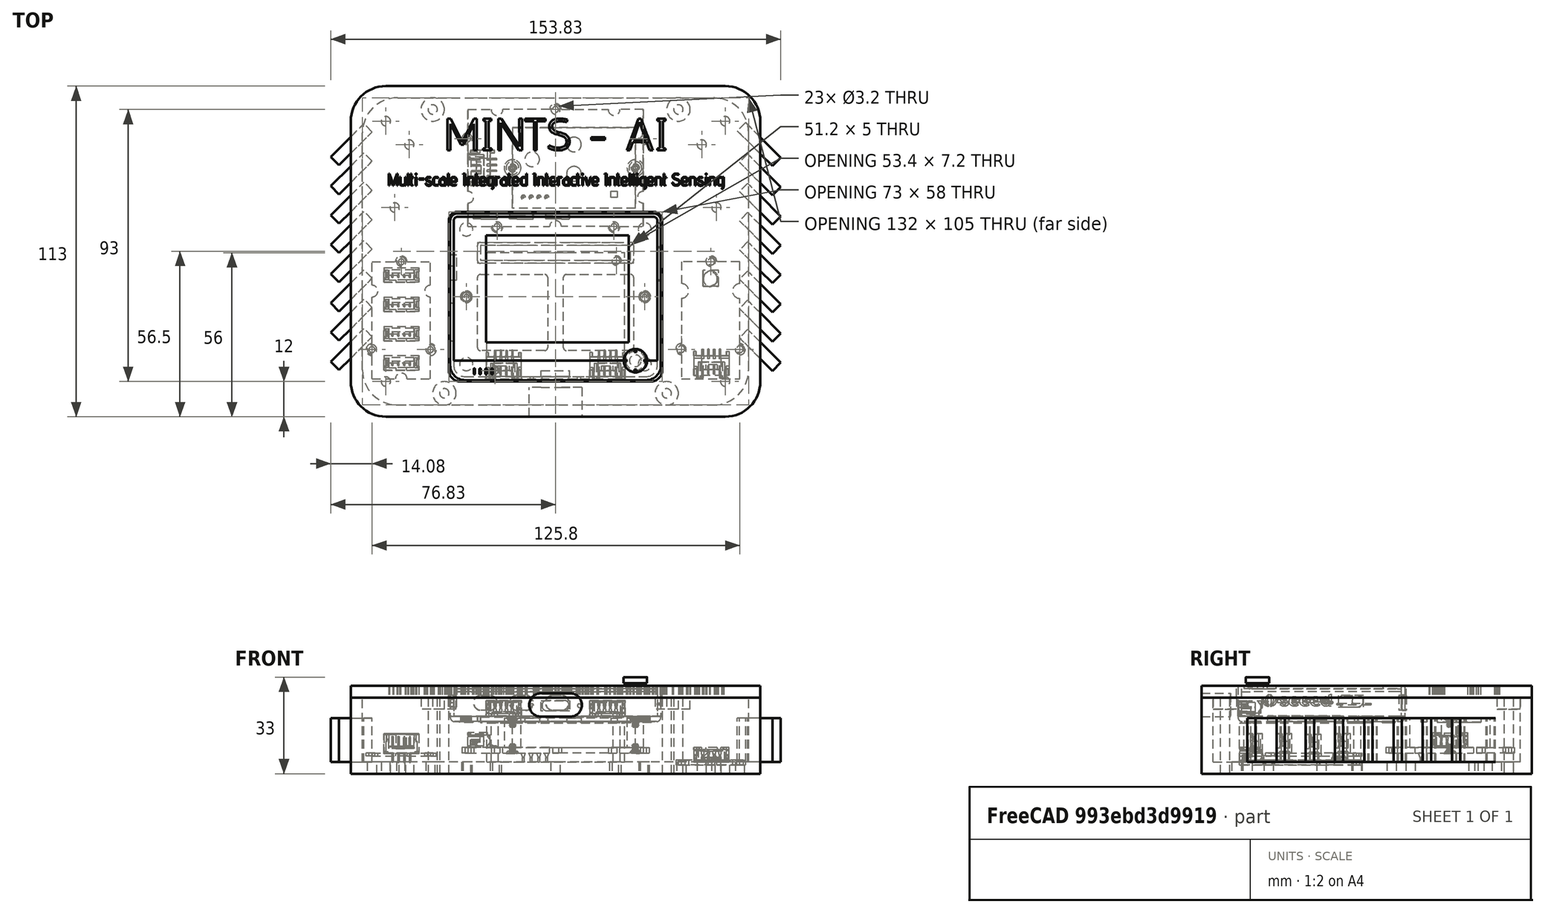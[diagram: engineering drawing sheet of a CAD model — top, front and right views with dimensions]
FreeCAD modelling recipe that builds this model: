
FCSTD DOCUMENT  (FreeCAD 0.20R29177 (Git))
Label: outBuildCopy2
License: All rights reserved
LicenseURL: http://en.wikipedia.org/wiki/All_rights_reserved
objects: Part::Cylinder×59, Part::Box×43, Part::Cut×33, Part::MultiFuse×23, Part::Feature×4, Part::Part2DObjectPython×2, Part::Extrusion×2
note: 166 computed .brp shape members not serialized (recipe doc carries the construction recipe); baked Part::Feature solids carry a one-line shape summary decoded from their .brp

FEATURE [Part::Feature] Feature  label="Grove I2C hub"
  Placement = pos=(15,60,9) rot=(0,0,1;3.14159rad)
  shape: bbox 24 x 42 x 9.849 mm, 365 faces, 5 solids (baked)
FEATURE [Part::Feature] Feature001  label="Grove_BME280"
  Placement = pos=(113,14,3) rot=(0.57735,0.57735,0.57735;2.0944rad)
  shape: bbox 23.8 x 41.9 x 6.016 mm, 221 faces, 2 solids (baked)
FEATURE [Part::Box] Box043  label="ips7100"
  AttacherType = Attacher::AttachEngine3D
  Height = 13.4
  Length = 47.1
  Width = 43.1
FEATURE [Part::Cylinder] Cylinder045  label="Cylinder"
  Angle = 360
  AttacherType = Attacher::AttachEngine3D
  FirstAngle = 0
  Height = 20
  Placement = pos=(2.75,2.75,0) rot=(0,0,1;0rad)
  Radius = 1.2
  SecondAngle = 0
FEATURE [Part::Cylinder] Cylinder046
  Angle = 360
  AttacherType = Attacher::AttachEngine3D
  FirstAngle = 0
  Height = 20
  Placement = pos=(44.35,40.35,0) rot=(0,0,1;0rad)
  Radius = 1.2
  SecondAngle = 0
FEATURE [Part::MultiFuse] Fusion030
  Shapes = -> [Cylinder045,Cylinder046]
FEATURE [Part::Cut] Cut012  label="ips7100s"
  Base = -> Box043
  Placement = pos=(46.5,13,4) rot=(0,0,1;0rad)
  Tool = -> Fusion030
FEATURE [Part::Feature] Feature002  label="Wio Terminal"
  Placement = pos=(70,41,30) rot=(0,0,1;0rad)
  shape: bbox 73.03 x 57.91 x 15.61 mm, 2405 faces, 30 solids (baked)
FEATURE [Part::Feature] Feature003  label="Seed Grove SCD30"
  Placement = pos=(40,65,9) rot=(1,0,0;4.71239rad)
  shape: bbox 64 x 44 x 15.1 mm, 422 faces, 13 solids (baked)
FEATURE [Part::Box] Box  label="base"
  AttacherType = Attacher::AttachEngine3D
  Height = 4
  Length = 140
  Width = 113
FEATURE [Part::Cylinder] Cylinder047  label="Cylinder048"
  Angle = 360
  AttacherType = Attacher::AttachEngine3D
  FirstAngle = 0
  Height = 10
  Placement = pos=(7.25,23,0) rot=(0,0,1;0rad)
  Radius = 1.6
  SecondAngle = 0
FEATURE [Part::Cylinder] Cylinder048  label="Cylinder049"
  Angle = 360
  AttacherType = Attacher::AttachEngine3D
  FirstAngle = 0
  Height = 10
  Placement = pos=(27.25,23,0) rot=(0,0,1;0rad)
  Radius = 1.6
  SecondAngle = 0
FEATURE [Part::Cylinder] Cylinder049  label="Cylinder050"
  Angle = 360
  AttacherType = Attacher::AttachEngine3D
  FirstAngle = 0
  Height = 10
  Placement = pos=(17.25,53,0) rot=(0,0,1;0rad)
  Radius = 1.6
  SecondAngle = 0
FEATURE [Part::MultiFuse] Fusion  label="i2cCuts"
  Shapes = -> [Cylinder047,Cylinder048,Cylinder049]
FEATURE [Part::Cylinder] Cylinder050  label="Cylinder051"
  Angle = 360
  AttacherType = Attacher::AttachEngine3D
  FirstAngle = 0
  Height = 10
  Placement = pos=(7.25,23,0) rot=(0,0,1;0rad)
  Radius = 1.6
  SecondAngle = 0
FEATURE [Part::Cylinder] Cylinder051  label="Cylinder052"
  Angle = 360
  AttacherType = Attacher::AttachEngine3D
  FirstAngle = 0
  Height = 10
  Placement = pos=(27.25,23,0) rot=(0,0,1;0rad)
  Radius = 1.6
  SecondAngle = 0
FEATURE [Part::Cylinder] Cylinder052  label="Cylinder053"
  Angle = 360
  AttacherType = Attacher::AttachEngine3D
  FirstAngle = 0
  Height = 10
  Placement = pos=(17.25,53,0) rot=(0,0,1;0rad)
  Radius = 1.6
  SecondAngle = 0
FEATURE [Part::MultiFuse] Fusion031  label="scdCuts001"
  Placement = pos=(105.8,0,0) rot=(0,0,1;0rad)
  Shapes = -> [Cylinder050,Cylinder051,Cylinder052]
FEATURE [Part::Cylinder] Cylinder053  label="Cylinder054"
  Angle = 360
  AttacherType = Attacher::AttachEngine3D
  FirstAngle = 0
  Height = 20
  Placement = pos=(2.75,2.75,0) rot=(0,0,1;0rad)
  Radius = 1.6
  SecondAngle = 0
FEATURE [Part::Cylinder] Cylinder054  label="Cylinder055"
  Angle = 360
  AttacherType = Attacher::AttachEngine3D
  FirstAngle = 0
  Height = 20
  Placement = pos=(44.35,40.35,0) rot=(0,0,1;0rad)
  Radius = 1.6
  SecondAngle = 0
FEATURE [Part::MultiFuse] Fusion032  label="ipsCuts"
  Placement = pos=(46.5,13,0) rot=(0,0,1;0rad)
  Shapes = -> [Cylinder053,Cylinder054]
FEATURE [Part::Cylinder] Cylinder055  label="Cylinder056"
  Angle = 360
  AttacherType = Attacher::AttachEngine3D
  FirstAngle = 0
  Height = 10
  Placement = pos=(50,65,0) rot=(0,0,1;0rad)
  Radius = 1.6
  SecondAngle = 0
FEATURE [Part::Cylinder] Cylinder056  label="Cylinder057"
  Angle = 360
  AttacherType = Attacher::AttachEngine3D
  FirstAngle = 0
  Height = 10
  Placement = pos=(90,65,0) rot=(0,0,1;0rad)
  Radius = 1.6
  SecondAngle = 0
FEATURE [Part::Cylinder] Cylinder057  label="Cylinder058"
  Angle = 360
  AttacherType = Attacher::AttachEngine3D
  FirstAngle = 0
  Height = 10
  Placement = pos=(100,95,0) rot=(0,0,1;0rad)
  Radius = 1.6
  SecondAngle = 0
FEATURE [Part::Cylinder] Cylinder058  label="Cylinder059"
  Angle = 360
  AttacherType = Attacher::AttachEngine3D
  FirstAngle = 0
  Height = 10
  Placement = pos=(40,95,0) rot=(0,0,1;0rad)
  Radius = 1.6
  SecondAngle = 0
FEATURE [Part::Cylinder] Cylinder059  label="Cylinder060"
  Angle = 360
  AttacherType = Attacher::AttachEngine3D
  FirstAngle = 0
  Height = 10
  Placement = pos=(70,105,0) rot=(0,0,1;0rad)
  Radius = 1.6
  SecondAngle = 0
FEATURE [Part::MultiFuse] Fusion033  label="scdCuts"
  Shapes = -> [Cylinder055,Cylinder056,Cylinder057,Cylinder058,Cylinder059]
FEATURE [Part::Cylinder] Cylinder060  label="Cylinder061"
  Angle = 360
  AttacherType = Attacher::AttachEngine3D
  FirstAngle = 0
  Height = 20
  Placement = pos=(39.5,41,0) rot=(0,0,1;0rad)
  Radius = 1.6
  SecondAngle = 0
FEATURE [Part::Cylinder] Cylinder061  label="Cylinder062"
  Angle = 360
  AttacherType = Attacher::AttachEngine3D
  FirstAngle = 0
  Height = 20
  Placement = pos=(100.5,41,0) rot=(0,0,1;0rad)
  Radius = 1.6
  SecondAngle = 0
FEATURE [Part::MultiFuse] Fusion034  label="wioCuts"
  Shapes = -> [Cylinder060,Cylinder061]
FEATURE [Part::MultiFuse] Fusion035  label="cuts"
  Shapes = -> [Fusion,Fusion031,Fusion032,Fusion033,Fusion034]
FEATURE [Part::Cut] Cut  label="base001"
  Base = -> Box
  Tool = -> Fusion035
FEATURE [Part::Cylinder] Cylinder062  label="Cylinder063"
  Angle = 360
  AttacherType = Attacher::AttachEngine3D
  FirstAngle = 0
  Height = 10
  Placement = pos=(12,12,0) rot=(0,0,1;0rad)
  Radius = 1.6
  SecondAngle = 0
FEATURE [Part::Cylinder] Cylinder063  label="Cylinder064"
  Angle = 360
  AttacherType = Attacher::AttachEngine3D
  FirstAngle = 0
  Height = 10
  Placement = pos=(128,12,0) rot=(0,0,1;0rad)
  Radius = 1.6
  SecondAngle = 0
FEATURE [Part::Cylinder] Cylinder064  label="Cylinder065"
  Angle = 360
  AttacherType = Attacher::AttachEngine3D
  FirstAngle = 0
  Height = 10
  Placement = pos=(12,101,0) rot=(0,0,1;0rad)
  Radius = 1.6
  SecondAngle = 0
FEATURE [Part::Cylinder] Cylinder065  label="Cylinder066"
  Angle = 360
  AttacherType = Attacher::AttachEngine3D
  FirstAngle = 0
  Height = 10
  Placement = pos=(128,101,0) rot=(0,0,1;0rad)
  Radius = 1.6
  SecondAngle = 0
FEATURE [Part::MultiFuse] Fusion036  label="outerCuts"
  Shapes = -> [Cylinder062,Cylinder063,Cylinder064,Cylinder065]
FEATURE [Part::Cut] Cut013  label="base003"
  Base = -> Cut
  Tool = -> Fusion036
FEATURE [Part::Box] Box044  label="base002"
  AttacherType = Attacher::AttachEngine3D
  Height = 4
  Length = 12
  Width = 12
FEATURE [Part::Cylinder] Cylinder  label="Cylinder067"
  Angle = 360
  AttacherType = Attacher::AttachEngine3D
  FirstAngle = 0
  Height = 10
  Placement = pos=(12,12,0) rot=(0,-0.707107,0.707107;0rad)
  Radius = 12
  SecondAngle = 0
FEATURE [Part::Cut] Cut014  label="cutOut"
  Base = -> Box044
  Tool = -> Cylinder
FEATURE [Part::Box] Box045  label="base004"
  AttacherType = Attacher::AttachEngine3D
  Height = 4
  Length = 12
  Width = 12
FEATURE [Part::Cylinder] Cylinder066  label="Cylinder068"
  Angle = 360
  AttacherType = Attacher::AttachEngine3D
  FirstAngle = 0
  Height = 10
  Placement = pos=(12,12,0) rot=(0,-0.707107,0.707107;0rad)
  Radius = 12
  SecondAngle = 0
FEATURE [Part::Cut] Cut015  label="cutOut001"
  Base = -> Box045
  Placement = pos=(140,-5.2e-15,0) rot=(0,0,1;1.5708rad)
  Tool = -> Cylinder066
FEATURE [Part::Box] Box046  label="base005"
  AttacherType = Attacher::AttachEngine3D
  Height = 4
  Length = 12
  Width = 12
FEATURE [Part::Cylinder] Cylinder067  label="Cylinder069"
  Angle = 360
  AttacherType = Attacher::AttachEngine3D
  FirstAngle = 0
  Height = 10
  Placement = pos=(12,12,0) rot=(0,-0.707107,0.707107;0rad)
  Radius = 12
  SecondAngle = 0
FEATURE [Part::Cut] Cut016  label="cutOut002"
  Base = -> Box046
  Placement = pos=(140,113,0) rot=(0,0,1;3.14159rad)
  Tool = -> Cylinder067
FEATURE [Part::Box] Box047  label="base006"
  AttacherType = Attacher::AttachEngine3D
  Height = 4
  Length = 12
  Width = 12
FEATURE [Part::Cylinder] Cylinder068  label="Cylinder070"
  Angle = 360
  AttacherType = Attacher::AttachEngine3D
  FirstAngle = 0
  Height = 10
  Placement = pos=(12,12,0) rot=(0,-0.707107,0.707107;0rad)
  Radius = 12
  SecondAngle = 0
FEATURE [Part::Cut] Cut017  label="cutOut003"
  Base = -> Box047
  Placement = pos=(0,113,0) rot=(0,0,1;4.71239rad)
  Tool = -> Cylinder068
FEATURE [Part::MultiFuse] Fusion037  label="cutOut004"
  Shapes = -> [Cut014,Cut015,Cut016,Cut017]
FEATURE [Part::Cut] Cut018
  Base = -> Cut013
  Tool = -> Fusion037
FEATURE [Part::Cylinder] Cylinder069  label="Cylinder071"
  Angle = 360
  AttacherType = Attacher::AttachEngine3D
  FirstAngle = 0
  Height = 10
  Placement = pos=(15,71.5,0) rot=(0,0,1;0rad)
  Radius = 1.6
  SecondAngle = 0
FEATURE [Part::Cylinder] Cylinder070  label="Cylinder072"
  Angle = 360
  AttacherType = Attacher::AttachEngine3D
  FirstAngle = 0
  Height = 10
  Placement = pos=(125,71.5,0) rot=(0,0,1;0rad)
  Radius = 1.6
  SecondAngle = 0
FEATURE [Part::MultiFuse] Fusion038  label="cuts001"
  Shapes = -> [Cylinder069,Cylinder070]
FEATURE [Part::Cut] Cut019  label="base007"
  Base = -> Cut018
  Tool = -> Fusion038
FEATURE [Part::Cylinder] Cylinder071  label="Cylinder073"
  Angle = 360
  AttacherType = Attacher::AttachEngine3D
  FirstAngle = 0
  Height = 10
  Placement = pos=(20,93,0) rot=(0,0,1;0rad)
  Radius = 1.6
  SecondAngle = 0
FEATURE [Part::Cylinder] Cylinder072  label="Cylinder074"
  Angle = 360
  AttacherType = Attacher::AttachEngine3D
  FirstAngle = 0
  Height = 10
  Placement = pos=(120,93,0) rot=(0,0,1;0rad)
  Radius = 1.6
  SecondAngle = 0
FEATURE [Part::MultiFuse] Fusion039  label="wallMounts"
  Shapes = -> [Cylinder071,Cylinder072]
FEATURE [Part::Cut] Cut020  label="base008"
  Base = -> Cut019
  Tool = -> Fusion039
FEATURE [Part::Box] Box048  label="top"
  AttacherType = Attacher::AttachEngine3D
  Height = 4
  Length = 140
  Width = 113
FEATURE [Part::Box] Box049  label="base009"
  AttacherType = Attacher::AttachEngine3D
  Height = 4
  Length = 12
  Width = 12
FEATURE [Part::Box] Box050  label="base010"
  AttacherType = Attacher::AttachEngine3D
  Height = 4
  Length = 12
  Width = 12
FEATURE [Part::Box] Box051  label="base011"
  AttacherType = Attacher::AttachEngine3D
  Height = 4
  Length = 12
  Width = 12
FEATURE [Part::Box] Box052  label="base012"
  AttacherType = Attacher::AttachEngine3D
  Height = 4
  Length = 12
  Width = 12
FEATURE [Part::Cylinder] Cylinder073  label="Cylinder075"
  Angle = 360
  AttacherType = Attacher::AttachEngine3D
  FirstAngle = 0
  Height = 10
  Placement = pos=(12,12,0) rot=(0,-0.707107,0.707107;0rad)
  Radius = 12
  SecondAngle = 0
FEATURE [Part::Cut] Cut021  label="cutOut005"
  Base = -> Box049
  Tool = -> Cylinder073
FEATURE [Part::Cylinder] Cylinder074  label="Cylinder076"
  Angle = 360
  AttacherType = Attacher::AttachEngine3D
  FirstAngle = 0
  Height = 10
  Placement = pos=(12,12,0) rot=(0,-0.707107,0.707107;0rad)
  Radius = 12
  SecondAngle = 0
FEATURE [Part::Cut] Cut022  label="cutOut006"
  Base = -> Box050
  Placement = pos=(140,-5.2e-15,0) rot=(0,0,1;1.5708rad)
  Tool = -> Cylinder074
FEATURE [Part::Cylinder] Cylinder075  label="Cylinder077"
  Angle = 360
  AttacherType = Attacher::AttachEngine3D
  FirstAngle = 0
  Height = 10
  Placement = pos=(12,12,0) rot=(0,-0.707107,0.707107;0rad)
  Radius = 12
  SecondAngle = 0
FEATURE [Part::Cut] Cut023  label="cutOut007"
  Base = -> Box051
  Placement = pos=(140,113,0) rot=(0,0,1;3.14159rad)
  Tool = -> Cylinder075
FEATURE [Part::Cylinder] Cylinder076  label="Cylinder078"
  Angle = 360
  AttacherType = Attacher::AttachEngine3D
  FirstAngle = 0
  Height = 10
  Placement = pos=(12,12,0) rot=(0,-0.707107,0.707107;0rad)
  Radius = 12
  SecondAngle = 0
FEATURE [Part::Cut] Cut024  label="cutOut008"
  Base = -> Box052
  Placement = pos=(0,113,0) rot=(0,0,-1;1.5708rad)
  Tool = -> Cylinder076
FEATURE [Part::MultiFuse] Fusion040  label="cutOut009"
  Shapes = -> [Cut021,Cut022,Cut023,Cut024]
FEATURE [Part::Cut] Cut025  label="top001"
  Base = -> Box048
  Placement = pos=(0,0,26) rot=(0,0,1;0rad)
  Tool = -> Fusion040
FEATURE [Part::Box] Box053  label="Cube"
  AttacherType = Attacher::AttachEngine3D
  Height = 10
  Length = 73
  Placement = pos=(33.5,12,26) rot=(0,0,1;0rad)
  Width = 58
FEATURE [Part::Box] Box054  label="Cube001"
  AttacherType = Attacher::AttachEngine3D
  Height = 10
  Length = 3
  Placement = pos=(33.5,67,26) rot=(0,0,1;0rad)
  Width = 3
FEATURE [Part::Cylinder] Cylinder077  label="Cylinder079"
  Angle = 360
  AttacherType = Attacher::AttachEngine3D
  FirstAngle = 0
  Height = 10
  Placement = pos=(36.5,67,26) rot=(0,0,1;0rad)
  Radius = 3
  SecondAngle = 0
FEATURE [Part::Cut] Cut026  label="outCutsDisplay"
  Base = -> Box054
  Tool = -> Cylinder077
FEATURE [Part::Box] Box055  label="Cube002"
  AttacherType = Attacher::AttachEngine3D
  Height = 10
  Length = 3
  Placement = pos=(33.5,67,26) rot=(0,0,1;0rad)
  Width = 3
FEATURE [Part::Cylinder] Cylinder078  label="Cylinder080"
  Angle = 360
  AttacherType = Attacher::AttachEngine3D
  FirstAngle = 0
  Height = 10
  Placement = pos=(36.5,67,26) rot=(0,0,1;0rad)
  Radius = 3
  SecondAngle = 0
FEATURE [Part::Cut] Cut027  label="outCutsDisplay001"
  Base = -> Box055
  Placement = pos=(36.5,103.5,0) rot=(0,0,1;4.71239rad)
  Tool = -> Cylinder078
FEATURE [Part::Box] Box057  label="Cube004"
  AttacherType = Attacher::AttachEngine3D
  Height = 10
  Length = 4
  Placement = pos=(32.5,67,26) rot=(0,0,1;0rad)
  Width = 4
FEATURE [Part::Cylinder] Cylinder080  label="Cylinder082"
  Angle = 360
  AttacherType = Attacher::AttachEngine3D
  FirstAngle = 0
  Height = 10
  Placement = pos=(36.5,67,26) rot=(0,0,1;0rad)
  Radius = 4
  SecondAngle = 0
FEATURE [Part::Cut] Cut029  label="outCutsDisplay003"
  Base = -> Box057
  Placement = pos=(104.5,-20.5,0) rot=(0,0,1;1.5708rad)
  Tool = -> Cylinder080
FEATURE [Part::Box] Box058  label="Cube005"
  AttacherType = Attacher::AttachEngine3D
  Height = 10
  Length = 4
  Placement = pos=(32.5,67,26) rot=(0,0,1;0rad)
  Width = 4
FEATURE [Part::Cylinder] Cylinder081  label="Cylinder083"
  Angle = 360
  AttacherType = Attacher::AttachEngine3D
  FirstAngle = 0
  Height = 10
  Placement = pos=(36.5,67,26) rot=(0,0,1;0rad)
  Radius = 4
  SecondAngle = 0
FEATURE [Part::Cut] Cut030  label="outCutsDisplay004"
  Base = -> Box058
  Placement = pos=(139,83,0) rot=(0,0,1;3.14159rad)
  Tool = -> Cylinder081
FEATURE [Part::MultiFuse] Fusion041  label="displayCuts"
  Shapes = -> [Cut029,Cut030,Cut026,Cut027]
FEATURE [Part::Cut] Cut031  label="topCut"
  Base = -> Box053
  Tool = -> Fusion041
FEATURE [Part::Cut] Cut032  label="top002"
  Base = -> Cut025
  Tool = -> Cut031
FEATURE [Part::Box] Box059  label="base013"
  AttacherType = Attacher::AttachEngine3D
  Height = 26
  Length = 140
  Width = 113
FEATURE [Part::Box] Box060  label="base014"
  AttacherType = Attacher::AttachEngine3D
  Height = 26
  Length = 12
  Width = 12
FEATURE [Part::Box] Box061  label="base015"
  AttacherType = Attacher::AttachEngine3D
  Height = 26
  Length = 12
  Width = 12
FEATURE [Part::Box] Box062  label="base016"
  AttacherType = Attacher::AttachEngine3D
  Height = 26
  Length = 12
  Width = 12
FEATURE [Part::Box] Box063  label="base017"
  AttacherType = Attacher::AttachEngine3D
  Height = 26
  Length = 12
  Width = 12
FEATURE [Part::Cylinder] Cylinder082  label="Cylinder084"
  Angle = 360
  AttacherType = Attacher::AttachEngine3D
  FirstAngle = 0
  Height = 26
  Placement = pos=(12,12,0) rot=(0,-0.707107,0.707107;0rad)
  Radius = 12
  SecondAngle = 0
FEATURE [Part::Cut] Cut033  label="cutOut010"
  Base = -> Box060
  Tool = -> Cylinder082
FEATURE [Part::Cylinder] Cylinder083  label="Cylinder085"
  Angle = 360
  AttacherType = Attacher::AttachEngine3D
  FirstAngle = 0
  Height = 26
  Placement = pos=(12,12,0) rot=(0,-0.707107,0.707107;0rad)
  Radius = 12
  SecondAngle = 0
FEATURE [Part::Cut] Cut034  label="cutOut011"
  Base = -> Box061
  Placement = pos=(140,-5.2e-15,0) rot=(0,0,1;1.5708rad)
  Tool = -> Cylinder083
FEATURE [Part::Cylinder] Cylinder084  label="Cylinder086"
  Angle = 360
  AttacherType = Attacher::AttachEngine3D
  FirstAngle = 0
  Height = 26
  Placement = pos=(12,12,0) rot=(0,-0.707107,0.707107;0rad)
  Radius = 12
  SecondAngle = 0
FEATURE [Part::Cut] Cut035  label="cutOut012"
  Base = -> Box062
  Placement = pos=(140,113,0) rot=(0,0,1;3.14159rad)
  Tool = -> Cylinder084
FEATURE [Part::Cylinder] Cylinder085  label="Cylinder087"
  Angle = 360
  AttacherType = Attacher::AttachEngine3D
  FirstAngle = 0
  Height = 26
  Placement = pos=(12,12,0) rot=(0,-0.707107,0.707107;0rad)
  Radius = 12
  SecondAngle = 0
FEATURE [Part::Cut] Cut036  label="cutOut013"
  Base = -> Box063
  Placement = pos=(0,113,0) rot=(0,0,-1;1.5708rad)
  Tool = -> Cylinder085
FEATURE [Part::MultiFuse] Fusion042  label="cuts002"
  Shapes = -> [Cut036,Cut033,Cut034,Cut035]
FEATURE [Part::Cut] Cut037  label="wall"
  Base = -> Box059
  Tool = -> Fusion042
FEATURE [Part::Box] Box064  label="base018"
  AttacherType = Attacher::AttachEngine3D
  Height = 26
  Length = 132
  Placement = pos=(4,4,0) rot=(0,0,1;0rad)
  Width = 105
FEATURE [Part::Box] Box065  label="base019"
  AttacherType = Attacher::AttachEngine3D
  Height = 26
  Length = 12
  Width = 12
FEATURE [Part::Box] Box066  label="base020"
  AttacherType = Attacher::AttachEngine3D
  Height = 26
  Length = 12
  Width = 12
FEATURE [Part::Box] Box067  label="base021"
  AttacherType = Attacher::AttachEngine3D
  Height = 26
  Length = 12
  Width = 12
FEATURE [Part::Box] Box068  label="base022"
  AttacherType = Attacher::AttachEngine3D
  Height = 26
  Length = 12
  Width = 12
FEATURE [Part::Cylinder] Cylinder086  label="Cylinder088"
  Angle = 360
  AttacherType = Attacher::AttachEngine3D
  FirstAngle = 0
  Height = 26
  Placement = pos=(12,12,0) rot=(0,-0.707107,0.707107;0rad)
  Radius = 12
  SecondAngle = 0
FEATURE [Part::Cut] Cut038  label="cutOut014"
  Base = -> Box065
  Placement = pos=(4,4,0) rot=(0,0,1;0rad)
  Tool = -> Cylinder086
FEATURE [Part::Cylinder] Cylinder087  label="Cylinder089"
  Angle = 360
  AttacherType = Attacher::AttachEngine3D
  FirstAngle = 0
  Height = 26
  Placement = pos=(12,12,0) rot=(0,-0.707107,0.707107;0rad)
  Radius = 12
  SecondAngle = 0
FEATURE [Part::Cut] Cut039  label="cutOut015"
  Base = -> Box066
  Placement = pos=(136,4,0) rot=(0,0,1;1.5708rad)
  Tool = -> Cylinder087
FEATURE [Part::Cylinder] Cylinder088  label="Cylinder090"
  Angle = 360
  AttacherType = Attacher::AttachEngine3D
  FirstAngle = 0
  Height = 26
  Placement = pos=(12,12,0) rot=(0,-0.707107,0.707107;0rad)
  Radius = 12
  SecondAngle = 0
FEATURE [Part::Cut] Cut040  label="cutOut016"
  Base = -> Box067
  Placement = pos=(136,109,0) rot=(0,0,1;3.14159rad)
  Tool = -> Cylinder088
FEATURE [Part::Cylinder] Cylinder089  label="Cylinder091"
  Angle = 360
  AttacherType = Attacher::AttachEngine3D
  FirstAngle = 0
  Height = 26
  Placement = pos=(12,12,0) rot=(0,-0.707107,0.707107;0rad)
  Radius = 12
  SecondAngle = 0
FEATURE [Part::Cut] Cut041  label="cutOut017"
  Base = -> Box068
  Placement = pos=(4,109,0) rot=(0,0,-1;1.5708rad)
  Tool = -> Cylinder089
FEATURE [Part::MultiFuse] Fusion043  label="cuts003"
  Shapes = -> [Cut041,Cut038,Cut039,Cut040]
FEATURE [Part::Cut] Cut042  label="wallCut"
  Base = -> Box064
  Tool = -> Fusion043
FEATURE [Part::Cut] Cut043  label="wall001-Base"
  Base = -> Cut037
  Tool = -> Cut042
FEATURE [Part::Cylinder] Cylinder091  label="Cylinder093"
  Angle = 360
  AttacherType = Attacher::AttachEngine3D
  FirstAngle = 0
  Height = 4
  Placement = pos=(108,8,0) rot=(0,0,1;0rad)
  Radius = 4
  SecondAngle = 0
FEATURE [Part::Cylinder] Cylinder092  label="Cylinder094"
  Angle = 360
  AttacherType = Attacher::AttachEngine3D
  FirstAngle = 0
  Height = 4
  Placement = pos=(32,8,0) rot=(0,0,1;0rad)
  Radius = 4
  SecondAngle = 0
FEATURE [Part::Cylinder] Cylinder093  label="Cylinder095"
  Angle = 360
  AttacherType = Attacher::AttachEngine3D
  FirstAngle = 0
  Height = 4
  Placement = pos=(112,105,0) rot=(0,0,1;0rad)
  Radius = 4
  SecondAngle = 0
FEATURE [Part::Cylinder] Cylinder094  label="Cylinder096"
  Angle = 360
  AttacherType = Attacher::AttachEngine3D
  FirstAngle = 0
  Height = 4
  Placement = pos=(28,105,0) rot=(0,0,1;0rad)
  Radius = 4
  SecondAngle = 0
FEATURE [Part::MultiFuse] Fusion044  label="topMountIns"
  Placement = pos=(0,0,22) rot=(0,0,1;0rad)
  Shapes = -> [Cylinder091,Cylinder092,Cylinder093,Cylinder094]
FEATURE [Part::Cylinder] Cylinder095  label="Cylinder097"
  Angle = 360
  AttacherType = Attacher::AttachEngine3D
  FirstAngle = 0
  Height = 26
  Placement = pos=(108,8,0) rot=(0,0,1;0rad)
  Radius = 1.6
  SecondAngle = 0
FEATURE [Part::Cylinder] Cylinder096  label="Cylinder098"
  Angle = 360
  AttacherType = Attacher::AttachEngine3D
  FirstAngle = 0
  Height = 26
  Placement = pos=(32,8,0) rot=(0,0,1;0rad)
  Radius = 1.6
  SecondAngle = 0
FEATURE [Part::Cylinder] Cylinder097  label="Cylinder099"
  Angle = 360
  AttacherType = Attacher::AttachEngine3D
  FirstAngle = 0
  Height = 26
  Placement = pos=(112,105,0) rot=(0,0,1;0rad)
  Radius = 1.6
  SecondAngle = 0
FEATURE [Part::Cylinder] Cylinder098  label="Cylinder100"
  Angle = 360
  AttacherType = Attacher::AttachEngine3D
  FirstAngle = 0
  Height = 26
  Placement = pos=(28,105,0) rot=(0,0,1;0rad)
  Radius = 1.6
  SecondAngle = 0
FEATURE [Part::MultiFuse] Fusion045  label="bottomCuts-base"
  Shapes = -> [Cylinder095,Cylinder096,Cylinder097,Cylinder098]
FEATURE [Part::Cylinder] Cylinder099  label="Cylinder101"
  Angle = 360
  AttacherType = Attacher::AttachEngine3D
  FirstAngle = 0
  Height = 26
  Placement = pos=(108,8,0) rot=(0,0,1;0rad)
  Radius = 1.6
  SecondAngle = 0
FEATURE [Part::Cylinder] Cylinder100  label="Cylinder102"
  Angle = 360
  AttacherType = Attacher::AttachEngine3D
  FirstAngle = 0
  Height = 26
  Placement = pos=(32,8,0) rot=(0,0,1;0rad)
  Radius = 1.6
  SecondAngle = 0
FEATURE [Part::Cylinder] Cylinder101  label="Cylinder103"
  Angle = 360
  AttacherType = Attacher::AttachEngine3D
  FirstAngle = 0
  Height = 26
  Placement = pos=(112,105,0) rot=(0,0,1;0rad)
  Radius = 1.6
  SecondAngle = 0
FEATURE [Part::Cylinder] Cylinder102  label="Cylinder104"
  Angle = 360
  AttacherType = Attacher::AttachEngine3D
  FirstAngle = 0
  Height = 26
  Placement = pos=(28,105,0) rot=(0,0,1;0rad)
  Radius = 1.6
  SecondAngle = 0
FEATURE [Part::MultiFuse] Fusion046  label="topMountCuts"
  Shapes = -> [Cylinder099,Cylinder100,Cylinder101,Cylinder102]
FEATURE [Part::Box] Box069  label="usbCCut"
  AttacherType = Attacher::AttachEngine3D
  Height = 8
  Length = 10
  Placement = pos=(65,0,19.5) rot=(0,0,1;0rad)
  Width = 10
FEATURE [Part::Cylinder] Cylinder103  label="usbCCut001"
  Angle = 360
  AttacherType = Attacher::AttachEngine3D
  FirstAngle = 0
  Height = 10
  Placement = pos=(65,10,23.5) rot=(1,0,0;1.5708rad)
  Radius = 4
  SecondAngle = 0
FEATURE [Part::Cylinder] Cylinder104  label="usbCCut002"
  Angle = 360
  AttacherType = Attacher::AttachEngine3D
  FirstAngle = 0
  Height = 10
  Placement = pos=(75,10,23.5) rot=(1,0,0;1.5708rad)
  Radius = 4
  SecondAngle = 0
FEATURE [Part::MultiFuse] Fusion047  label="usbCCut003"
  Shapes = -> [Box069,Cylinder103,Cylinder104]
FEATURE [Part::Box] Box070  label="ventCut"
  AttacherType = Attacher::AttachEngine3D
  Height = 15
  Length = 16
  Placement = pos=(-4,16,0) rot=(0,0,1;0.785398rad)
  Width = 4
FEATURE [Part::Box] Box071  label="ventCut001"
  AttacherType = Attacher::AttachEngine3D
  Height = 15
  Length = 16
  Placement = pos=(-4,36,0) rot=(0,0,1;0.785398rad)
  Width = 4
FEATURE [Part::Box] Box072  label="ventCut002"
  AttacherType = Attacher::AttachEngine3D
  Height = 15
  Length = 16
  Placement = pos=(-4,26,0) rot=(0,0,1;0.785398rad)
  Width = 4
FEATURE [Part::Box] Box073  label="ventCut003"
  AttacherType = Attacher::AttachEngine3D
  Height = 15
  Length = 16
  Placement = pos=(-4,46,0) rot=(0,0,1;0.785398rad)
  Width = 4
FEATURE [Part::Box] Box074  label="ventCut004"
  AttacherType = Attacher::AttachEngine3D
  Height = 15
  Length = 16
  Placement = pos=(-4,56,0) rot=(0,0,1;0.785398rad)
  Width = 4
FEATURE [Part::Box] Box075  label="ventCut005"
  AttacherType = Attacher::AttachEngine3D
  Height = 15
  Length = 16
  Placement = pos=(-4,66,0) rot=(0,0,1;0.785398rad)
  Width = 4
FEATURE [Part::Box] Box076  label="ventCut006"
  AttacherType = Attacher::AttachEngine3D
  Height = 15
  Length = 16
  Placement = pos=(-4,76,0) rot=(0,0,1;0.785398rad)
  Width = 4
FEATURE [Part::Box] Box077  label="ventCut007"
  AttacherType = Attacher::AttachEngine3D
  Height = 15
  Length = 16
  Placement = pos=(-4,86,0) rot=(0,0,1;0.785398rad)
  Width = 4
FEATURE [Part::MultiFuse] Fusion048  label="leftVents-base"
  Placement = pos=(0,0,4) rot=(0,0,1;0rad)
  Shapes = -> [Box070,Box071,Box072,Box073,Box074,Box075,Box076,Box077]
FEATURE [Part::Box] Box078  label="ventCut008"
  AttacherType = Attacher::AttachEngine3D
  Height = 15
  Length = 16
  Placement = pos=(-4,16,0) rot=(0,0,1;2.35619rad)
  Width = 4
FEATURE [Part::Box] Box079  label="ventCut009"
  AttacherType = Attacher::AttachEngine3D
  Height = 15
  Length = 16
  Placement = pos=(-4,36,0) rot=(0,0,1;2.35619rad)
  Width = 4
FEATURE [Part::Box] Box080  label="ventCut010"
  AttacherType = Attacher::AttachEngine3D
  Height = 15
  Length = 16
  Placement = pos=(-4,26,0) rot=(0,0,1;2.35619rad)
  Width = 4
FEATURE [Part::Box] Box081  label="ventCut011"
  AttacherType = Attacher::AttachEngine3D
  Height = 15
  Length = 16
  Placement = pos=(-4,46,0) rot=(0,0,1;2.35619rad)
  Width = 4
FEATURE [Part::Box] Box082  label="ventCut012"
  AttacherType = Attacher::AttachEngine3D
  Height = 15
  Length = 16
  Placement = pos=(-4,56,0) rot=(0,0,1;2.35619rad)
  Width = 4
FEATURE [Part::Box] Box083  label="ventCut013"
  AttacherType = Attacher::AttachEngine3D
  Height = 15
  Length = 16
  Placement = pos=(-4,66,0) rot=(0,0,1;2.35619rad)
  Width = 4
FEATURE [Part::Box] Box084  label="ventCut014"
  AttacherType = Attacher::AttachEngine3D
  Height = 15
  Length = 16
  Placement = pos=(-4,76,0) rot=(0,0,1;2.35619rad)
  Width = 4
FEATURE [Part::Box] Box085  label="ventCut015"
  AttacherType = Attacher::AttachEngine3D
  Height = 15
  Length = 17
  Placement = pos=(-4,86,0) rot=(0,0,1;2.35619rad)
  Width = 4
FEATURE [Part::MultiFuse] Fusion049  label="rightVents001-base"
  Placement = pos=(151,2.5,4) rot=(0,0,1;0rad)
  Shapes = -> [Box078,Box079,Box080,Box081,Box082,Box083,Box084,Box085]
FEATURE [Part::Part2DObjectPython] ShapeString  # Draft 2D object (typed FeaturePython)
  FontFile = <userpath>/Downloads/AnticSans-Regular.otf
  MakeFace = true
  Placement = pos=(32,92,0) rot=(0,0,1;0rad)
  Size = 5
  String = MINTS - AI
  Tracking = 0
FEATURE [Part::Part2DObjectPython] ShapeString001  # Draft 2D object (typed FeaturePython)
  FontFile = <userpath>/Downloads/adventpro-regular.ttf
  MakeFace = true
  Placement = pos=(12.5,81,0) rot=(0,0,1;0rad)
  Size = 2.25
  String = Multi-scale Integrated Interactive Intelligent Sensing
  Tracking = 0
FEATURE [Part::Extrusion] Extrude001
  Base = -> ShapeString
  Dir = (0,0,-1)
  DirMode = 0
  FaceMakerClass = Part::FaceMakerBullseye
  LengthFwd = 10
  LengthRev = 0
  Placement = pos=(0,-1,30.5) rot=(0,0,1;0rad)
  Solid = false
  Symmetric = false
FEATURE [Part::Extrusion] Extrude002
  Base = -> ShapeString001
  Dir = (0,0,-1)
  DirMode = 0
  FaceMakerClass = Part::FaceMakerBullseye
  LengthFwd = 10
  LengthRev = 0
  Placement = pos=(0,-2,30.5) rot=(0,0,1;0rad)
  Solid = false
  Symmetric = false
FEATURE [Part::MultiFuse] Fusion050  label="textCuts"
  Shapes = -> [Extrude001,Extrude002]
FEATURE [Part::Cut] Cut044  label="top003"
  Base = -> Cut032
  Tool = -> Fusion050
FEATURE [Part::MultiFuse] Fusion051  label="base023"
  Shapes = -> [Cut020,Cut043]
